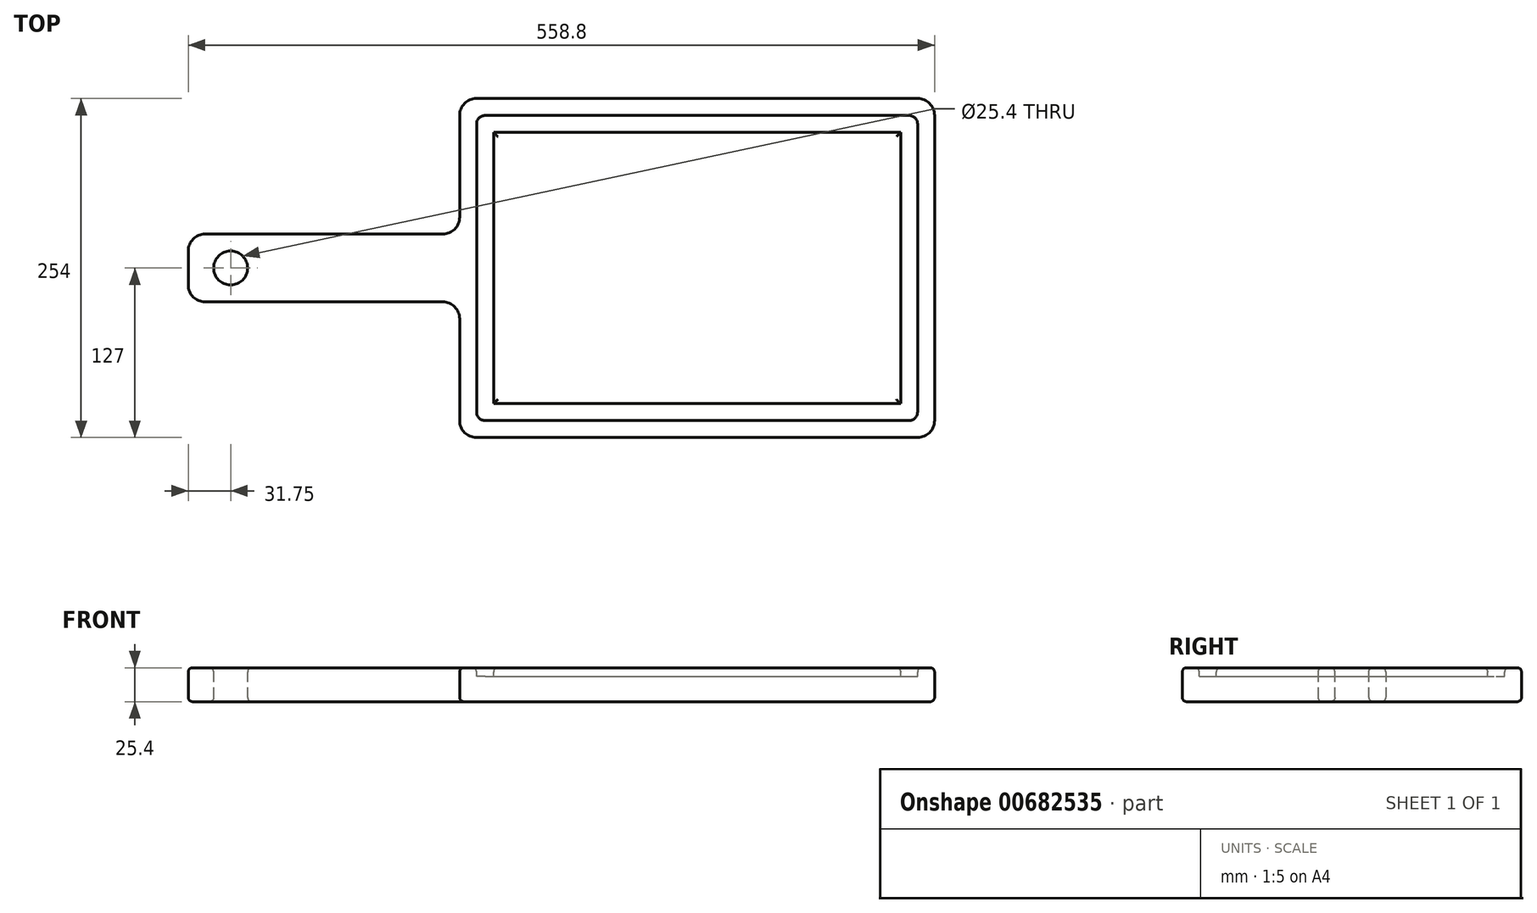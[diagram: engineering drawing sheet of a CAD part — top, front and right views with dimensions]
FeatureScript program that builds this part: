
annotation { "Feature Type Name" : "Feature", "Feature Type Description" : "" }
export const myFeature = defineFeature(function(context is Context, id is Id, definition is map)
    precondition{}
    {
        {
            var Q0;
            Q0=qCreatedBy(makeId("Top.planeOp"),FACE);
            var sketch = newSketch(context, id + "F0", { "sketchPlane" : qUnion([Q0])});
            skLineSegment(sketch, "E0.bottom", {"start": v(0, 0) * mm, "end": v(355.6, 0) * mm});
            skLineSegment(sketch, "E0.top", {"start": v(0, 254) * mm, "end": v(355.6, 254) * mm});
            skLineSegment(sketch, "E0.left", {"start": v(0, 0) * mm, "end": v(0, 254) * mm});
            skLineSegment(sketch, "E0.right", {"start": v(355.6, 0) * mm, "end": v(355.6, 254) * mm});
            skLineSegment(sketch, "E1.bottom", {"start": v(0, 101.6) * mm, "end": v(-203.2, 101.6) * mm});
            skLineSegment(sketch, "E1.top", {"start": v(0, 152.4) * mm, "end": v(-203.2, 152.4) * mm});
            skLineSegment(sketch, "E1.left", {"start": v(0, 101.6) * mm, "end": v(0, 152.4) * mm});
            skLineSegment(sketch, "E1.right", {"start": v(-203.2, 101.6) * mm, "end": v(-203.2, 152.4) * mm});
            skSolve(sketch);
        }
        {
            var Q0;
            {var subQ3=sQuery(id+"F0.wireOp",EDGE,"E0.bottom");Q0=makeQuery(id+"F0.imprint","IMPRINT",FACE,{"disambiguationData":[TD([[makeQuery(id+"F0.imprint","IMPRINT",EDGE,{"derivedFrom":subQ3}),1.0]])]});}
            var Q1;
            Q1=makeQuery(id+"F0.imprint","IMPRINT",FACE,{"disambiguationData":[TD([[makeQuery(id+"F0.imprint","IMPRINT",EDGE,{"derivedFrom":sQuery(id+"F0.wireOp",EDGE,"E1.bottom")}),-1.0]])]});
            extrude(context, id + "F1", {"entities" : qUnion([Q0, Q1]), "depth" : 25.4 * mm, "offsetDistance" : 25.4 * mm});
        }
        {
            var Q0;
            Q0=makeQuery(id+"F1.opExtrude","CAP_FACE",FACE,{"disambiguationData":[OSD([sQuery(id+"F0.wireOp",EDGE,"E0.bottom"),sQuery(id+"F0.wireOp",EDGE,"E0.top"),sQuery(id+"F0.wireOp",EDGE,"E0.left"),sQuery(id+"F0.wireOp",EDGE,"E0.right"),sQuery(id+"F0.wireOp",EDGE,"E1.bottom"),sQuery(id+"F0.wireOp",EDGE,"E1.top"),sQuery(id+"F0.wireOp",EDGE,"E1.right")])],"isStart":false});
            var sketch = newSketch(context, id + "F2", { "sketchPlane" : qUnion([Q0])});
            skCircle(sketch, "E2", {"center": v(-171.45, 127) * mm, "radius": 12.7 * mm});
            skSolve(sketch);
        }
        {
            var Q0;
            Q0 = qSketchRegion(id + "F2", true);
            extrude(context, id + "F3", {"entities" : qUnion([Q0]), "operationType" : NewBodyOperationType.REMOVE, "oppositeDirection" : true, "depth" : 25.4 * mm, "offsetDistance" : 25.4 * mm});
        }
        {
            var Q0;
            Q0=makeQuery(id+"F1.opExtrude","CAP_FACE",FACE,{"disambiguationData":[OSD([sQuery(id+"F0.wireOp",EDGE,"E0.bottom"),sQuery(id+"F0.wireOp",EDGE,"E0.top"),sQuery(id+"F0.wireOp",EDGE,"E0.left"),sQuery(id+"F0.wireOp",EDGE,"E0.right"),sQuery(id+"F0.wireOp",EDGE,"E1.bottom"),sQuery(id+"F0.wireOp",EDGE,"E1.top"),sQuery(id+"F0.wireOp",EDGE,"E1.right")])],"isStart":false});
            var sketch = newSketch(context, id + "F4", { "sketchPlane" : qUnion([Q0])});
            skLineSegment(sketch, "E3.0", {"start": v(12.7, 12.7) * mm, "end": v(12.7, 101.6) * mm});
            skLineSegment(sketch, "E3.1", {"start": v(12.7, 152.4) * mm, "end": v(12.7, 241.3) * mm});
            skLineSegment(sketch, "E3.2", {"start": v(12.7, 241.3) * mm, "end": v(342.9, 241.3) * mm});
            skLineSegment(sketch, "E3.3", {"start": v(342.9, 12.7) * mm, "end": v(342.9, 241.3) * mm});
            skLineSegment(sketch, "E3.4", {"start": v(12.7, 12.7) * mm, "end": v(342.9, 12.7) * mm});
            skLineSegment(sketch, "E4", {"start": v(12.7, 152.4) * mm, "end": v(12.7, 101.6) * mm});
            skLineSegment(sketch, "E5.0", {"start": v(25.4, 152.4) * mm, "end": v(25.4, 228.6) * mm});
            skLineSegment(sketch, "E5.1", {"start": v(330.2, 25.4) * mm, "end": v(330.2, 228.6) * mm});
            skLineSegment(sketch, "E5.2", {"start": v(25.4, 25.4) * mm, "end": v(330.2, 25.4) * mm});
            skLineSegment(sketch, "E5.3", {"start": v(25.4, 228.6) * mm, "end": v(330.2, 228.6) * mm});
            skLineSegment(sketch, "E5.4", {"start": v(25.4, 25.4) * mm, "end": v(25.4, 101.6) * mm});
            skLineSegment(sketch, "E5.5", {"start": v(25.4, 152.4) * mm, "end": v(25.4, 101.6) * mm});
            skSolve(sketch);
        }
        {
            var Q0;
            Q0=makeQuery(id+"F4.imprint","IMPRINT",FACE,{"disambiguationData":[TD([[makeQuery(id+"F4.imprint","IMPRINT",EDGE,{"derivedFrom":sQuery(id+"F4.wireOp",EDGE,"E3.0")}),-1.0]])]});
            extrude(context, id + "F5", {"entities" : qUnion([Q0]), "operationType" : NewBodyOperationType.REMOVE, "oppositeDirection" : true, "depth" : 6.35 * mm, "offsetDistance" : 25.4 * mm});
        }
        {
            var Q0;
            Q0=makeQuery(id+"F5.boolean.opBoolean","COPY",EDGE,{"derivedFrom":makeQuery(id+"F5.opExtrude","SWEPT_EDGE",EDGE,{"disambiguationData":[OSD([sQuery(id+"F4.wireOp",EDGE,"E3.1"),sQuery(id+"F4.wireOp",EDGE,"E3.2")])]})});
            var Q1;
            Q1=makeQuery(id+"F5.boolean.opBoolean","COPY",EDGE,{"derivedFrom":makeQuery(id+"F5.opExtrude","SWEPT_EDGE",EDGE,{"disambiguationData":[OSD([sQuery(id+"F4.wireOp",EDGE,"E3.0"),sQuery(id+"F4.wireOp",EDGE,"E3.4")])]})});
            var Q2;
            Q2=makeQuery(id+"F5.boolean.opBoolean","COPY",EDGE,{"derivedFrom":makeQuery(id+"F5.opExtrude","SWEPT_EDGE",EDGE,{"disambiguationData":[OSD([sQuery(id+"F4.wireOp",EDGE,"E3.2"),sQuery(id+"F4.wireOp",EDGE,"E3.3")])]})});
            var Q3;
            Q3=makeQuery(id+"F5.boolean.opBoolean","COPY",EDGE,{"derivedFrom":makeQuery(id+"F5.opExtrude","SWEPT_EDGE",EDGE,{"disambiguationData":[OSD([sQuery(id+"F4.wireOp",EDGE,"E3.3"),sQuery(id+"F4.wireOp",EDGE,"E3.4")])]})});
            fillet(context, id + "F6", {"entities" : qUnion([Q0, Q1, Q2, Q3]), "radius" : 6.35 * mm, "tangentPropagation" : true, "allowEdgeOverflow" : false});
        }
        {
            var Q0;
            Q0=makeQuery(id+"F1.opExtrude","SWEPT_EDGE",EDGE,{"disambiguationData":[OSD([sQuery(id+"F0.wireOp",EDGE,"E0.top"),sQuery(id+"F0.wireOp",EDGE,"E0.right")])]});
            var Q1;
            Q1=makeQuery(id+"F1.opExtrude","SWEPT_EDGE",EDGE,{"disambiguationData":[OSD([sQuery(id+"F0.wireOp",EDGE,"E0.top"),sQuery(id+"F0.wireOp",EDGE,"E0.left")])]});
            var Q2;
            Q2=makeQuery(id+"F1.opExtrude","SWEPT_EDGE",EDGE,{"disambiguationData":[OSD([sQuery(id+"F0.wireOp",EDGE,"E0.bottom"),sQuery(id+"F0.wireOp",EDGE,"E0.left")])]});
            var Q3;
            Q3=makeQuery(id+"F1.opExtrude","SWEPT_EDGE",EDGE,{"disambiguationData":[OSD([sQuery(id+"F0.wireOp",EDGE,"E0.bottom"),sQuery(id+"F0.wireOp",EDGE,"E0.right")])]});
            var Q4;
            Q4=makeQuery(id+"F1.opExtrude","SWEPT_EDGE",EDGE,{"disambiguationData":[OSD([sQuery(id+"F0.wireOp",EDGE,"E1.top"),sQuery(id+"F0.wireOp",EDGE,"E1.right")])]});
            var Q5;
            Q5=makeQuery(id+"F1.opExtrude","SWEPT_EDGE",EDGE,{"disambiguationData":[OSD([sQuery(id+"F0.wireOp",EDGE,"E1.bottom"),sQuery(id+"F0.wireOp",EDGE,"E1.right")])]});
            var Q6;
            Q6=makeQuery(id+"F1.opExtrude","SWEPT_EDGE",EDGE,{"disambiguationData":[OSD([sQuery(id+"F0.wireOp",EDGE,"E0.left"),sQuery(id+"F0.wireOp",EDGE,"E1.bottom"),sQuery(id+"F0.wireOp",EDGE,"E1.left")])]});
            var Q7;
            Q7=makeQuery(id+"F1.opExtrude","SWEPT_EDGE",EDGE,{"disambiguationData":[OSD([sQuery(id+"F0.wireOp",EDGE,"E0.left"),sQuery(id+"F0.wireOp",EDGE,"E1.top"),sQuery(id+"F0.wireOp",EDGE,"E1.left")])]});
            fillet(context, id + "F7", {"entities" : qUnion([Q0, Q1, Q2, Q3, Q4, Q5, Q6, Q7]), "radius" : 12.7 * mm, "tangentPropagation" : true, "allowEdgeOverflow" : false});
        }
        {
            var Q0;
            Q0=makeQuery(id+"F5.boolean.opBoolean","SPLIT",FACE,{"disambiguationData":[TD([makeQuery(id+"F5.opExtrude","SWEPT_FACE",FACE,{"disambiguationData":[OSD([sQuery(id+"F4.wireOp",EDGE,"E5.1")])]})])],"derivedFrom":makeQuery(id+"F1.opExtrude","CAP_FACE",FACE,{"disambiguationData":[OSD([sQuery(id+"F0.wireOp",EDGE,"E0.bottom"),sQuery(id+"F0.wireOp",EDGE,"E0.top"),sQuery(id+"F0.wireOp",EDGE,"E0.left"),sQuery(id+"F0.wireOp",EDGE,"E0.right"),sQuery(id+"F0.wireOp",EDGE,"E1.bottom"),sQuery(id+"F0.wireOp",EDGE,"E1.top"),sQuery(id+"F0.wireOp",EDGE,"E1.right")])],"isStart":false})});
            var Q1;
            {var subQ0=sQuery(id+"F0.wireOp",EDGE,"E0.left");var subQ1=sQuery(id+"F0.wireOp",EDGE,"E0.top");var subQ3=sQuery(id+"F0.wireOp",EDGE,"E1.top");var subQ4=sQuery(id+"F0.wireOp",EDGE,"E1.right");var subQ5=sQuery(id+"F0.wireOp",EDGE,"E1.bottom");var subQ6=sQuery(id+"F0.wireOp",EDGE,"E0.right");var subQ7=sQuery(id+"F0.wireOp",EDGE,"E0.bottom");Q1=makeQuery(id+"F5.boolean.opBoolean","SPLIT",FACE,{"disambiguationData":[TD([makeQuery(id+"F1.opExtrude","SWEPT_FACE",FACE,{"disambiguationData":[OSD([subQ7])]})])],"derivedFrom":makeQuery(id+"F1.opExtrude","CAP_FACE",FACE,{"disambiguationData":[OSD([subQ7,subQ1,subQ0,subQ6,subQ5,subQ3,subQ4])],"isStart":false})});}
            var Q2;
            Q2=makeQuery(id+"F1.opExtrude","CAP_FACE",FACE,{"disambiguationData":[OSD([sQuery(id+"F0.wireOp",EDGE,"E0.bottom"),sQuery(id+"F0.wireOp",EDGE,"E0.top"),sQuery(id+"F0.wireOp",EDGE,"E0.left"),sQuery(id+"F0.wireOp",EDGE,"E0.right"),sQuery(id+"F0.wireOp",EDGE,"E1.bottom"),sQuery(id+"F0.wireOp",EDGE,"E1.top"),sQuery(id+"F0.wireOp",EDGE,"E1.right")])],"isStart":true});
            fillet(context, id + "F8", {"entities" : qUnion([Q0, Q1, Q2]), "radius" : 3.17 * mm, "tangentPropagation" : true, "allowEdgeOverflow" : false});
        }
    });
